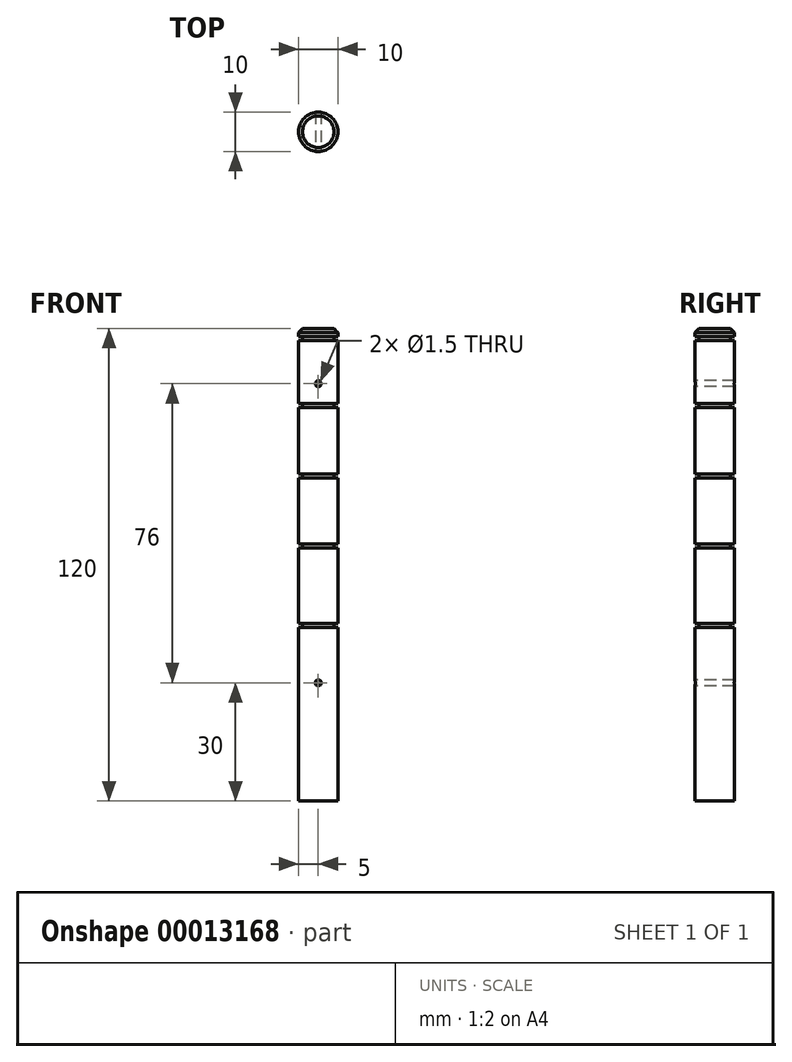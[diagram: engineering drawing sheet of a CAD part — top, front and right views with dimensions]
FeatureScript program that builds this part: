
annotation { "Feature Type Name" : "Feature", "Feature Type Description" : "" }
export const myFeature = defineFeature(function(context is Context, id is Id, definition is map)
    precondition{}
    {
        {
            var Q0;
            Q0=qCreatedBy(makeId("Top.planeOp"),FACE);
            var sketch = newSketch(context, id + "F0", { "sketchPlane" : qUnion([Q0])});
            skCircle(sketch, "E0", {"center": v(0, 0) * mm, "radius": 5 * mm});
            skSolve(sketch);
        }
        {
            var Q0;
            Q0=qSketchRegion(id+"F0",true);
            extrude(context, id + "F1", {"entities" : qUnion([Q0]), "oppositeDirection" : true, "depth" : 120 * mm});
        }
        {
            var Q0;
            Q0=makeQuery(id+"F1.opExtrude","CAP_EDGE",EDGE,{"disambiguationData":[OSD([sQuery(id+"F0.wireOp",EDGE,"E0")])],"isStart":true});
            chamfer(context, id + "F2", {"entities" : qUnion([Q0]), "width" : 1 * mm, "tangentPropagation" : true});
        }
        {
            var Q0;
            Q0=qCreatedBy(makeId("Front.planeOp"),FACE);
            var sketch = newSketch(context, id + "F3", { "sketchPlane" : qUnion([Q0])});
            skLineSegment(sketch, "E1", {"start": v(0, 0) * mm, "end": v(0, 28.37) * mm, "construction": true});
            skLineSegment(sketch, "E2.bottom", {"start": v(5, -3) * mm, "end": v(4, -3) * mm});
            skLineSegment(sketch, "E2.top", {"start": v(5, -2) * mm, "end": v(4, -2) * mm});
            skLineSegment(sketch, "E2.left", {"start": v(5, -3) * mm, "end": v(5, -2) * mm});
            skLineSegment(sketch, "E2.right", {"start": v(4, -3) * mm, "end": v(4, -2) * mm});
            skLineSegment(sketch, "E3.MirrorCS", {"start": v(-4, -3) * mm, "end": v(-4, -2) * mm, "construction": true});
            skLineSegment(sketch, "E4.MirrorCS", {"start": v(-5, -3) * mm, "end": v(-5, -2) * mm, "construction": true});
            skLineSegment(sketch, "E5.MirrorCS", {"start": v(-5, -2) * mm, "end": v(-4, -2) * mm, "construction": true});
            skLineSegment(sketch, "E6.MirrorCS", {"start": v(-5, -3) * mm, "end": v(-4, -3) * mm, "construction": true});
            skLineSegment(sketch, "E7.0", {"start": v(-5, -120) * mm, "end": v(5, -120) * mm, "construction": true});
            skLineSegment(sketch, "E8.bottom", {"start": v(5, -19) * mm, "end": v(4, -19) * mm});
            skLineSegment(sketch, "E8.top", {"start": v(5, -20) * mm, "end": v(4, -20) * mm});
            skLineSegment(sketch, "E8.left", {"start": v(5, -19) * mm, "end": v(5, -20) * mm});
            skLineSegment(sketch, "E8.right", {"start": v(4, -19) * mm, "end": v(4, -20) * mm});
            skLineSegment(sketch, "E9.bottom", {"start": v(5, -37) * mm, "end": v(4, -37) * mm});
            skLineSegment(sketch, "E9.top", {"start": v(5, -38) * mm, "end": v(4, -38) * mm});
            skLineSegment(sketch, "E9.left", {"start": v(5, -37) * mm, "end": v(5, -38) * mm});
            skLineSegment(sketch, "E9.right", {"start": v(4, -37) * mm, "end": v(4, -38) * mm});
            skLineSegment(sketch, "E10.bottom", {"start": v(5, -54.68) * mm, "end": v(4, -54.68) * mm});
            skLineSegment(sketch, "E10.top", {"start": v(5, -55.68) * mm, "end": v(4, -55.68) * mm});
            skLineSegment(sketch, "E10.left", {"start": v(5, -54.68) * mm, "end": v(5, -55.68) * mm});
            skLineSegment(sketch, "E10.right", {"start": v(4, -54.68) * mm, "end": v(4, -55.68) * mm});
            skLineSegment(sketch, "E11.bottom", {"start": v(5, -74.98) * mm, "end": v(4, -74.98) * mm});
            skLineSegment(sketch, "E11.top", {"start": v(5, -75.98) * mm, "end": v(4, -75.98) * mm});
            skLineSegment(sketch, "E11.left", {"start": v(5, -74.98) * mm, "end": v(5, -75.98) * mm});
            skLineSegment(sketch, "E11.right", {"start": v(4, -74.98) * mm, "end": v(4, -75.98) * mm});
            skSolve(sketch);
        }
        {
            var Q0;
            Q0=qSketchRegion(id+"F3",true);
            var Q1;
            Q1=sQuery(id+"F3.wireOp",EDGE,"E1");
            revolve(context, id + "F4", {"operationType" : NewBodyOperationType.REMOVE, "entities" : qUnion([Q0]), "axis" : qUnion([Q1]), "revolveType" : RevolveType.FULL, "oppositeDirection" : true});
        }
        {
            var Q0;
            Q0=qCreatedBy(makeId("Front.planeOp"),FACE);
            var sketch = newSketch(context, id + "F5", { "sketchPlane" : qUnion([Q0])});
            skCircle(sketch, "E12", {"center": v(0, -14) * mm, "radius": 0.75 * mm});
            skCircle(sketch, "E13", {"center": v(0, -90) * mm, "radius": 0.75 * mm});
            skSolve(sketch);
        }
        {
            var Q0;
            Q0=qSketchRegion(id+"F5",true);
            extrude(context, id + "F6", {"entities" : qUnion([Q0]), "operationType" : NewBodyOperationType.REMOVE, "endBound" : BoundingType.SYMMETRIC, "oppositeDirection" : true, "depth" : 25 * mm});
        }
    });
